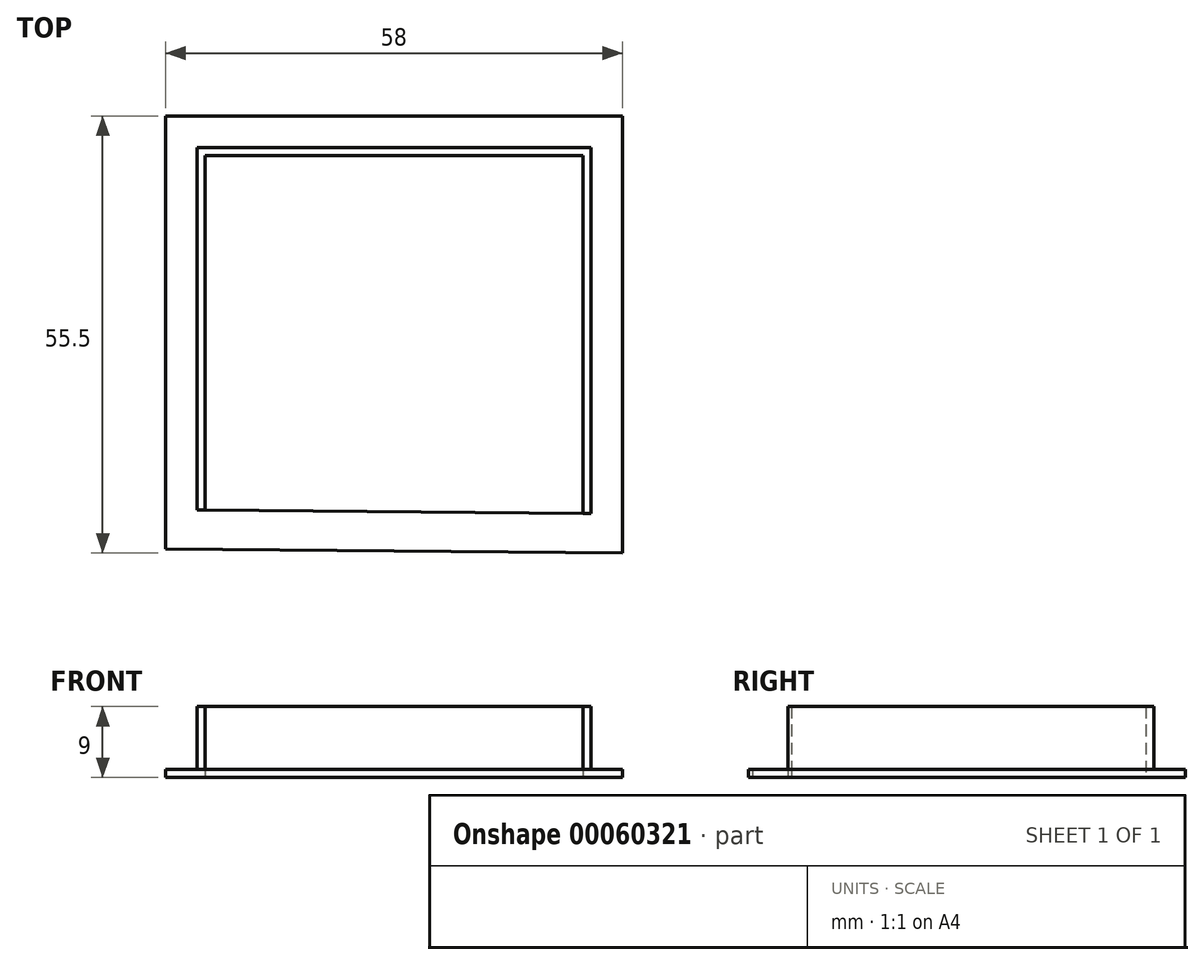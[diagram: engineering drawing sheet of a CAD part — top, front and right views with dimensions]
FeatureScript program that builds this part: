
annotation { "Feature Type Name" : "Feature", "Feature Type Description" : "" }
export const myFeature = defineFeature(function(context is Context, id is Id, definition is map)
    precondition{}
    {
        {
            var Q0;
            Q0=qCreatedBy(makeId("Top.planeOp"),FACE);
            var sketch = newSketch(context, id + "F0", { "sketchPlane" : qUnion([Q0])});
            skLineSegment(sketch, "E0.bottom", {"start": v(-24, 22.5) * mm, "end": v(24, 22.5) * mm});
            skLineSegment(sketch, "E0.left", {"start": v(-24, 22.5) * mm, "end": v(-24, -22.54) * mm});
            skLineSegment(sketch, "E0.right", {"start": v(24, 22.5) * mm, "end": v(24, -22.96) * mm});
            skLineSegment(sketch, "E1", {"start": v(0, 22.5) * mm, "end": v(0, -22.5) * mm, "construction": true});
            skLineSegment(sketch, "E2", {"start": v(-24, -0.02) * mm, "end": v(24, -0.23) * mm, "construction": true});
            skLineSegment(sketch, "E3", {"start": v(-24, -22.54) * mm, "end": v(24, -22.96) * mm});
            skLineSegment(sketch, "E4", {"start": v(-25, 23.5) * mm, "end": v(25, 23.5) * mm});
            skLineSegment(sketch, "E5", {"start": v(-29, 27.5) * mm, "end": v(29, 27.5) * mm});
            skLineSegment(sketch, "E6", {"start": v(-25, 23.5) * mm, "end": v(-25, -22.54) * mm});
            skLineSegment(sketch, "E7", {"start": v(25, 23.5) * mm, "end": v(25, -22.96) * mm});
            skLineSegment(sketch, "E8", {"start": v(29, -28) * mm, "end": v(-29, -27.5) * mm});
            skLineSegment(sketch, "E9", {"start": v(29, 27.5) * mm, "end": v(29, -28) * mm});
            skLineSegment(sketch, "E10", {"start": v(-29, 27.5) * mm, "end": v(-29, -27.5) * mm});
            skLineSegment(sketch, "E11", {"start": v(-24, -22.54) * mm, "end": v(-25, -22.54) * mm});
            skLineSegment(sketch, "E12", {"start": v(24, -22.96) * mm, "end": v(25, -22.96) * mm});
            skSolve(sketch);
        }
        {
            var Q0;
            Q0=makeQuery(id+"F0.imprint","IMPRINT",FACE,{"disambiguationData":[TD([[makeQuery(id+"F0.imprint","IMPRINT",EDGE,{"derivedFrom":sQuery(id+"F0.wireOp",EDGE,"E0.bottom")}),1.0]])]});
            extrude(context, id + "F1", {"entities" : qUnion([Q0]), "depth" : 9 * mm});
        }
        {
            var Q0;
            Q0=makeQuery(id+"F0.imprint","IMPRINT",FACE,{"disambiguationData":[TD([[makeQuery(id+"F0.imprint","IMPRINT",EDGE,{"derivedFrom":sQuery(id+"F0.wireOp",EDGE,"E4")}),1.0]])]});
            extrude(context, id + "F2", {"entities" : qUnion([Q0]), "operationType" : NewBodyOperationType.ADD, "depth" : 1 * mm});
        }
    });
